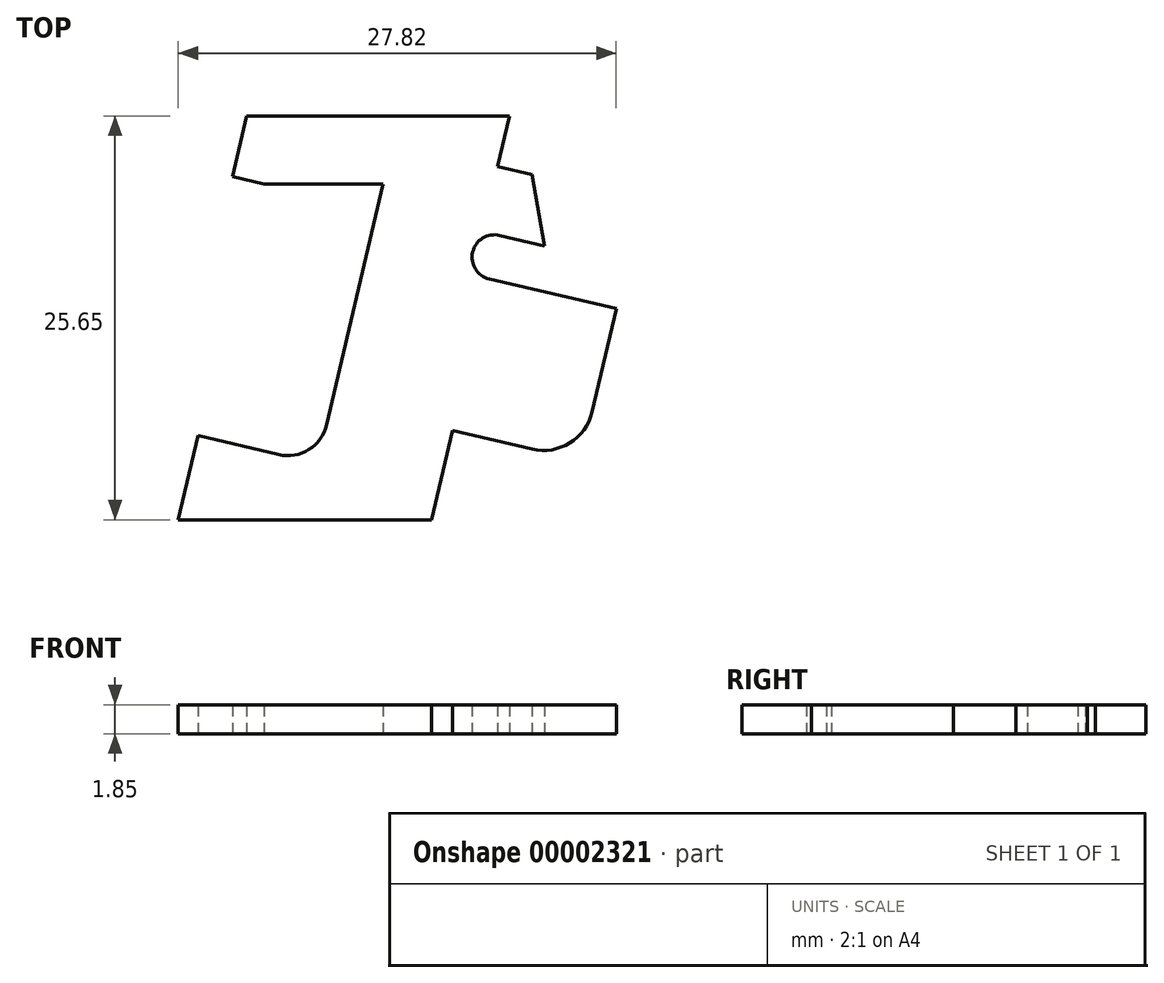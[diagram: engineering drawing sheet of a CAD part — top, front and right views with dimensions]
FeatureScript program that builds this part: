
annotation { "Feature Type Name" : "Feature", "Feature Type Description" : "" }
export const myFeature = defineFeature(function(context is Context, id is Id, definition is map)
    precondition{}
    {
        {
            var Q0;
            Q0=qCreatedBy(makeId("Top.planeOp"),FACE);
            var sketch = newSketch(context, id + "F0", { "sketchPlane" : qUnion([Q0])});
            skLineSegment(sketch, "E0", {"start": v(4.35, 25.65) * mm, "end": v(21.04, 25.65) * mm});
            skLineSegment(sketch, "E1", {"start": v(21.04, 25.65) * mm, "end": v(20.29, 22.43) * mm});
            skLineSegment(sketch, "E2", {"start": v(20.29, 22.43) * mm, "end": v(22.46, 21.92) * mm});
            skLineSegment(sketch, "E3", {"start": v(22.46, 21.92) * mm, "end": v(23.28, 17.4) * mm});
            skLineSegment(sketch, "E4", {"start": v(23.28, 17.4) * mm, "end": v(20.41, 18.07) * mm});
            skLineSegment(sketch, "E5", {"start": v(18.7, 17) * mm, "end": v(18.7, 17) * mm});
            skLineSegment(sketch, "E6", {"start": v(19.76, 15.3) * mm, "end": v(27.82, 13.4) * mm});
            skLineSegment(sketch, "E7", {"start": v(27.82, 13.4) * mm, "end": v(26.29, 6.85) * mm});
            skLineSegment(sketch, "E8", {"start": v(22.47, 4.49) * mm, "end": v(17.43, 5.67) * mm});
            skLineSegment(sketch, "E9", {"start": v(17.43, 5.67) * mm, "end": v(16.1, 0) * mm});
            skLineSegment(sketch, "E10", {"start": v(16.1, 0) * mm, "end": v(0, 0) * mm});
            skLineSegment(sketch, "E11", {"start": v(0, 0) * mm, "end": v(1.25, 5.34) * mm});
            skLineSegment(sketch, "E12", {"start": v(1.25, 5.34) * mm, "end": v(6.37, 4.14) * mm});
            skLineSegment(sketch, "E13", {"start": v(9.42, 6.03) * mm, "end": v(13, 21.31) * mm});
            skLineSegment(sketch, "E14", {"start": v(13, 21.31) * mm, "end": v(5.47, 21.31) * mm});
            skLineSegment(sketch, "E15", {"start": v(5.47, 21.31) * mm, "end": v(3.44, 21.79) * mm});
            skLineSegment(sketch, "E16", {"start": v(3.44, 21.79) * mm, "end": v(4.35, 25.65) * mm});
            skPoint(sketch, "E17.visualSharp", {"position": v(19.03, 18.4) * mm});
            skArc(sketch, "E17.filletArc", {"start": v(20.41, 18.07) * mm, "mid": v(19.34, 17.9) * mm, "end": v(18.7, 17) * mm});
            skPoint(sketch, "E18.visualSharp", {"position": v(18.38, 15.62) * mm});
            skArc(sketch, "E18.filletArc", {"start": v(18.7, 17) * mm, "mid": v(18.88, 15.93) * mm, "end": v(19.76, 15.3) * mm});
            skPoint(sketch, "E19.visualSharp", {"position": v(8.84, 3.56) * mm});
            skArc(sketch, "E19.filletArc", {"start": v(6.37, 4.14) * mm, "mid": v(8.3, 4.45) * mm, "end": v(9.42, 6.03) * mm});
            skPoint(sketch, "E20.visualSharp", {"position": v(25.56, 3.76) * mm});
            skArc(sketch, "E20.filletArc", {"start": v(22.47, 4.49) * mm, "mid": v(24.87, 4.88) * mm, "end": v(26.29, 6.85) * mm});
            skSolve(sketch);
        }
        {
            var Q0;
            Q0 = qSketchRegion(id + "F0", true);
            var Q1;
            Q1=makeQuery(id+"F0.imprint","IMPRINT",FACE,{"disambiguationData":[TD([[makeQuery(id+"F0.imprint","IMPRINT",EDGE,{"derivedFrom":sQuery(id+"F0.wireOp",EDGE,"E0")}),-1.0]])]});
            extrude(context, id + "F1", {"entities" : qUnion([Q0, Q1]), "depth" : 1.85 * mm});
        }
    });
